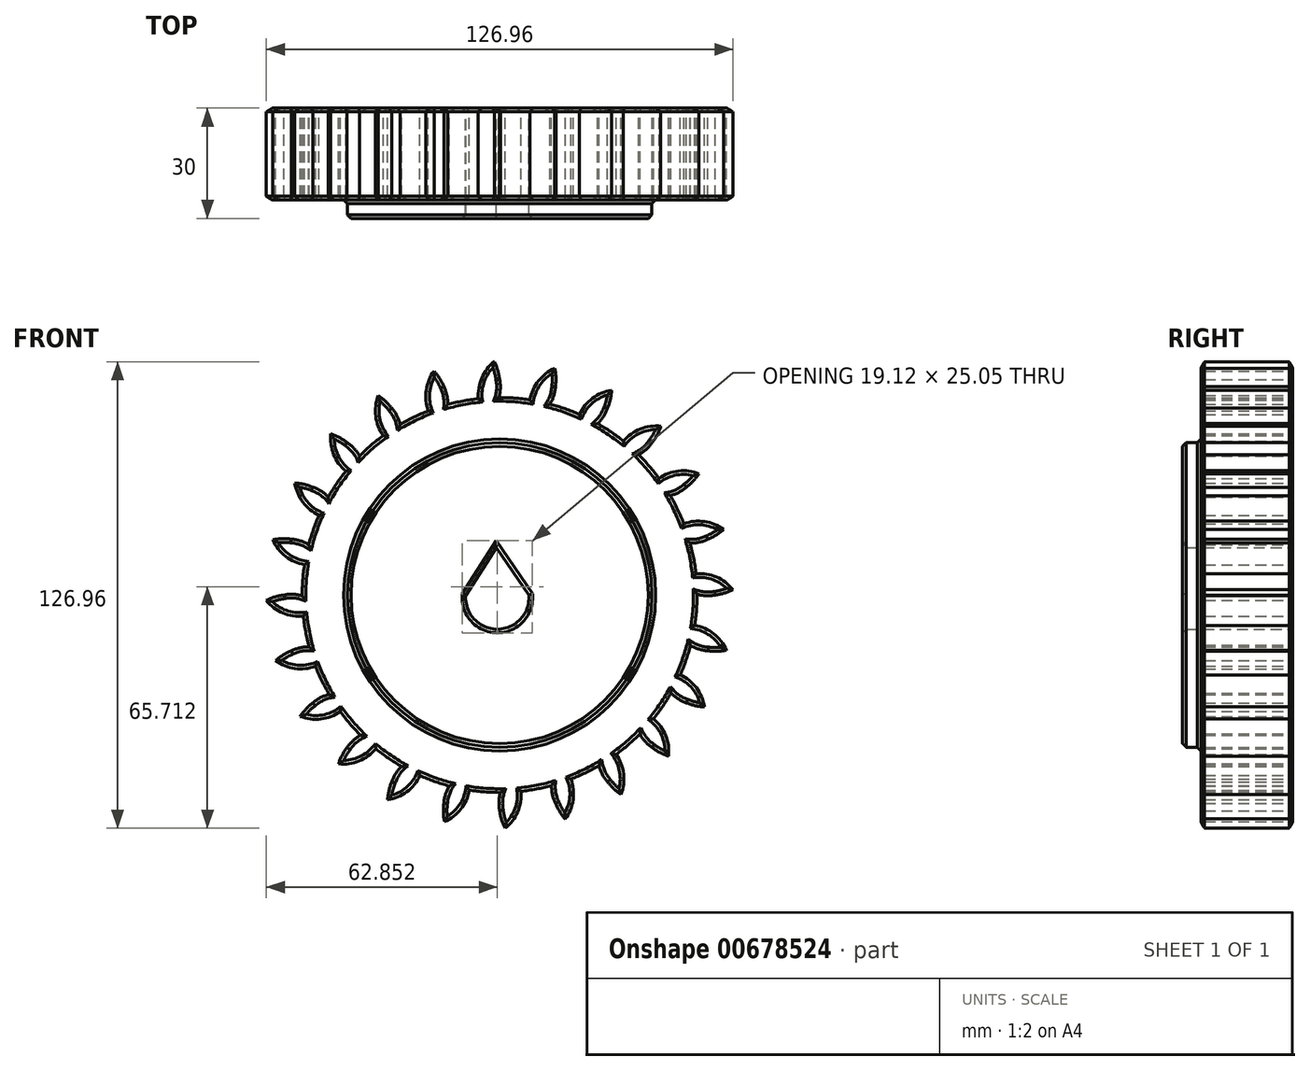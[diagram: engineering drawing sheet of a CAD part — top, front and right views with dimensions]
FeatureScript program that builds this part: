
annotation { "Feature Type Name" : "Feature", "Feature Type Description" : "" }
export const myFeature = defineFeature(function(context is Context, id is Id, definition is map)
    precondition{}
    {
        {
            var Q0;
            Q0=qCreatedBy(makeId("Front.planeOp"),FACE);
            var sketch = newSketch(context, id + "F0", { "sketchPlane" : qUnion([Q0])});
            skCircle(sketch, "E0", {"center": v(0, 0) * mm, "radius": 53.72 * mm});
            skCircle(sketch, "E1", {"center": v(0, 0) * mm, "radius": 58.67 * mm, "construction": true});
            skCircle(sketch, "E2", {"center": v(0, 0) * mm, "radius": 63.5 * mm, "construction": true});
            skLineSegment(sketch, "E3", {"start": v(0, 0) * mm, "end": v(0, 86.11) * mm, "construction": true});
            skLineSegment(sketch, "E4", {"start": v(0, 0) * mm, "end": v(-5.95, 90.7) * mm, "construction": true});
            skCircle(sketch, "E5", {"center": v(0, 58.67) * mm, "radius": 14.6 * mm, "construction": true});
            skLineSegment(sketch, "E6", {"start": v(0, 58.67) * mm, "end": v(-66.92, 58.67) * mm, "construction": true});
            skLineSegment(sketch, "E7", {"start": v(0, 58.67) * mm, "end": v(-68.71, 43.32) * mm, "construction": true});
            skCircle(sketch, "E8", {"center": v(-14.5, 56.86) * mm, "radius": 14.6 * mm, "construction": true});
            skArc(sketch, "E9", {"start": v(0, 58.67) * mm, "mid": v(-0.53, 61.14) * mm, "end": v(-1.48, 63.48) * mm});
            skArc(sketch, "E10", {"start": v(-0.23, 53.72) * mm, "mid": v(0.19, 56.18) * mm, "end": v(0, 58.67) * mm});
            skArc(sketch, "E11", {"start": v(-1.48, 63.48) * mm, "mid": v(-4.9, 58.99) * mm, "end": v(-5.76, 53.41) * mm});
            skCircle(sketch, "E12", {"center": v(0, 0) * mm, "radius": 41.43 * mm});
            skLineSegment(sketch, "E13", {"start": v(-9.22, 0) * mm, "end": v(-0.85, 12.95) * mm});
            skLineSegment(sketch, "E14", {"start": v(-0.85, 12.95) * mm, "end": v(7.96, 0) * mm});
            skArc(sketch, "E15", {"start": v(-9.22, 0) * mm, "mid": v(-0.63, -9.3) * mm, "end": v(7.96, 0) * mm});
            skSolve(sketch);
        }
        {
            var Q0;
            {var subQ0=sQuery(id+"F0.wireOp",EDGE,"E0");var subQ1=makeQuery(id+"F0.imprint","INTERSECT",VERTEX,{"derivedFrom":[subQ0,sQuery(id+"F0.wireOp",EDGE,"E10")]});Q0=makeQuery(id+"F0.imprint","IMPRINT",FACE,{"disambiguationData":[TD([[makeQuery(id+"F0.imprint","IMPRINT",EDGE,{"disambiguationData":[TD([[subQ1,-1.0]])],"derivedFrom":subQ0}),1.0]])]});}
            var Q1;
            Q1=makeQuery(id+"F0.imprint","IMPRINT",FACE,{"disambiguationData":[TD([[makeQuery(id+"F0.imprint","IMPRINT",EDGE,{"derivedFrom":sQuery(id+"F0.wireOp",EDGE,"E9")}),1.0]])]});
            extrude(context, id + "F1", {"entities" : qUnion([Q0, Q1]), "depth" : 25 * mm, "offsetDistance" : 25 * mm});
        }
        {
            var Q0;
            Q0=makeQuery(id+"F1.opExtrude","SWEPT_BODY",BODY,{"disambiguationData":[OSD([sQuery(id+"F0.wireOp",EDGE,"E0"),sQuery(id+"F0.wireOp",EDGE,"E9"),sQuery(id+"F0.wireOp",EDGE,"E10"),sQuery(id+"F0.wireOp",EDGE,"E11")])]});
            var Q1;
            Q1=makeQuery(id+"F1.opExtrude","SWEPT_FACE",FACE,{"disambiguationData":[OSD([sQuery(id+"F0.wireOp",EDGE,"E0")])]});
            circularPattern(context, id + "F2", {"entities" : qUnion([Q0]), "axis" : qUnion([Q1]), "angle" : 360 * degree, "instanceCount" : 24, "equalSpace" : true});
        }
        {
            var Q0;
            Q0=makeQuery(id+"F0.imprint","IMPRINT",FACE,{"disambiguationData":[TD([[makeQuery(id+"F0.imprint","IMPRINT",EDGE,{"derivedFrom":sQuery(id+"F0.wireOp",EDGE,"E12")}),1.0]])]});
            extrude(context, id + "F3", {"entities" : qUnion([Q0]), "operationType" : NewBodyOperationType.ADD, "depth" : 30 * mm, "offsetDistance" : 25 * mm});
        }
        {
            var Q0;
            Q0=makeQuery(id+"F3.opExtrude","CAP_FACE",FACE,{"disambiguationData":[OSD([sQuery(id+"F0.wireOp",EDGE,"E12"),sQuery(id+"F0.wireOp",EDGE,"E13"),sQuery(id+"F0.wireOp",EDGE,"E14"),sQuery(id+"F0.wireOp",EDGE,"E15")])],"isStart":false});
            chamfer(context, id + "F4", {"entities" : qUnion([Q0]), "width" : 1 * mm, "tangentPropagation" : true});
        }
        {
            var Q0;
            {var subQ0=makeQuery(id+"F1.opExtrude","CAP_FACE",FACE,{"disambiguationData":[OSD([sQuery(id+"F0.wireOp",EDGE,"E0"),sQuery(id+"F0.wireOp",EDGE,"E9"),sQuery(id+"F0.wireOp",EDGE,"E10"),sQuery(id+"F0.wireOp",EDGE,"E11"),sQuery(id+"F0.wireOp",EDGE,"E12")])],"isStart":false});Q0=makeQuery(id+"F3.boolean.opBoolean","MERGE",FACE,{"derivedFrom":[subQ0,makeQuery(id+"F2.opPattern","COPY",FACE,{"derivedFrom":subQ0,"instanceName":"1"}),makeQuery(id+"F2.opPattern","COPY",FACE,{"derivedFrom":subQ0,"instanceName":"2"}),makeQuery(id+"F2.opPattern","COPY",FACE,{"derivedFrom":subQ0,"instanceName":"3"}),makeQuery(id+"F2.opPattern","COPY",FACE,{"derivedFrom":subQ0,"instanceName":"4"}),makeQuery(id+"F2.opPattern","COPY",FACE,{"derivedFrom":subQ0,"instanceName":"5"}),makeQuery(id+"F2.opPattern","COPY",FACE,{"derivedFrom":subQ0,"instanceName":"6"}),makeQuery(id+"F2.opPattern","COPY",FACE,{"derivedFrom":subQ0,"instanceName":"7"}),makeQuery(id+"F2.opPattern","COPY",FACE,{"derivedFrom":subQ0,"instanceName":"8"}),makeQuery(id+"F2.opPattern","COPY",FACE,{"derivedFrom":subQ0,"instanceName":"9"}),makeQuery(id+"F2.opPattern","COPY",FACE,{"derivedFrom":subQ0,"instanceName":"10"}),makeQuery(id+"F2.opPattern","COPY",FACE,{"derivedFrom":subQ0,"instanceName":"11"}),makeQuery(id+"F2.opPattern","COPY",FACE,{"derivedFrom":subQ0,"instanceName":"12"}),makeQuery(id+"F2.opPattern","COPY",FACE,{"derivedFrom":subQ0,"instanceName":"13"}),makeQuery(id+"F2.opPattern","COPY",FACE,{"derivedFrom":subQ0,"instanceName":"14"}),makeQuery(id+"F2.opPattern","COPY",FACE,{"derivedFrom":subQ0,"instanceName":"15"}),makeQuery(id+"F2.opPattern","COPY",FACE,{"derivedFrom":subQ0,"instanceName":"16"}),makeQuery(id+"F2.opPattern","COPY",FACE,{"derivedFrom":subQ0,"instanceName":"17"}),makeQuery(id+"F2.opPattern","COPY",FACE,{"derivedFrom":subQ0,"instanceName":"18"}),makeQuery(id+"F2.opPattern","COPY",FACE,{"derivedFrom":subQ0,"instanceName":"19"}),makeQuery(id+"F2.opPattern","COPY",FACE,{"derivedFrom":subQ0,"instanceName":"20"}),makeQuery(id+"F2.opPattern","COPY",FACE,{"derivedFrom":subQ0,"instanceName":"21"}),makeQuery(id+"F2.opPattern","COPY",FACE,{"derivedFrom":subQ0,"instanceName":"22"}),makeQuery(id+"F2.opPattern","COPY",FACE,{"derivedFrom":subQ0,"instanceName":"23"})]});}
            var Q1;
            {var subQ0=sQuery(id+"F0.wireOp",EDGE,"E12");var subQ1=makeQuery(id+"F1.opExtrude","CAP_FACE",FACE,{"disambiguationData":[OSD([sQuery(id+"F0.wireOp",EDGE,"E0"),sQuery(id+"F0.wireOp",EDGE,"E9"),sQuery(id+"F0.wireOp",EDGE,"E10"),sQuery(id+"F0.wireOp",EDGE,"E11"),subQ0])],"isStart":true});Q1=makeQuery(id+"F3.boolean.opBoolean","MERGE",FACE,{"derivedFrom":[subQ1,makeQuery(id+"F2.opPattern","COPY",FACE,{"derivedFrom":subQ1,"instanceName":"1"}),makeQuery(id+"F2.opPattern","COPY",FACE,{"derivedFrom":subQ1,"instanceName":"2"}),makeQuery(id+"F2.opPattern","COPY",FACE,{"derivedFrom":subQ1,"instanceName":"3"}),makeQuery(id+"F2.opPattern","COPY",FACE,{"derivedFrom":subQ1,"instanceName":"4"}),makeQuery(id+"F2.opPattern","COPY",FACE,{"derivedFrom":subQ1,"instanceName":"5"}),makeQuery(id+"F2.opPattern","COPY",FACE,{"derivedFrom":subQ1,"instanceName":"6"}),makeQuery(id+"F2.opPattern","COPY",FACE,{"derivedFrom":subQ1,"instanceName":"7"}),makeQuery(id+"F2.opPattern","COPY",FACE,{"derivedFrom":subQ1,"instanceName":"8"}),makeQuery(id+"F2.opPattern","COPY",FACE,{"derivedFrom":subQ1,"instanceName":"9"}),makeQuery(id+"F2.opPattern","COPY",FACE,{"derivedFrom":subQ1,"instanceName":"10"}),makeQuery(id+"F2.opPattern","COPY",FACE,{"derivedFrom":subQ1,"instanceName":"11"}),makeQuery(id+"F2.opPattern","COPY",FACE,{"derivedFrom":subQ1,"instanceName":"12"}),makeQuery(id+"F2.opPattern","COPY",FACE,{"derivedFrom":subQ1,"instanceName":"13"}),makeQuery(id+"F2.opPattern","COPY",FACE,{"derivedFrom":subQ1,"instanceName":"14"}),makeQuery(id+"F2.opPattern","COPY",FACE,{"derivedFrom":subQ1,"instanceName":"15"}),makeQuery(id+"F2.opPattern","COPY",FACE,{"derivedFrom":subQ1,"instanceName":"16"}),makeQuery(id+"F2.opPattern","COPY",FACE,{"derivedFrom":subQ1,"instanceName":"17"}),makeQuery(id+"F2.opPattern","COPY",FACE,{"derivedFrom":subQ1,"instanceName":"18"}),makeQuery(id+"F2.opPattern","COPY",FACE,{"derivedFrom":subQ1,"instanceName":"19"}),makeQuery(id+"F2.opPattern","COPY",FACE,{"derivedFrom":subQ1,"instanceName":"20"}),makeQuery(id+"F2.opPattern","COPY",FACE,{"derivedFrom":subQ1,"instanceName":"21"}),makeQuery(id+"F2.opPattern","COPY",FACE,{"derivedFrom":subQ1,"instanceName":"22"}),makeQuery(id+"F2.opPattern","COPY",FACE,{"derivedFrom":subQ1,"instanceName":"23"}),makeQuery(id+"F3.opExtrude","CAP_FACE",FACE,{"disambiguationData":[OSD([subQ0,sQuery(id+"F0.wireOp",EDGE,"E13"),sQuery(id+"F0.wireOp",EDGE,"E14"),sQuery(id+"F0.wireOp",EDGE,"E15")])],"isStart":true})]});}
            chamfer(context, id + "F5", {"entities" : qUnion([Q0, Q1]), "width" : 1 * mm, "tangentPropagation" : true});
        }
    });
